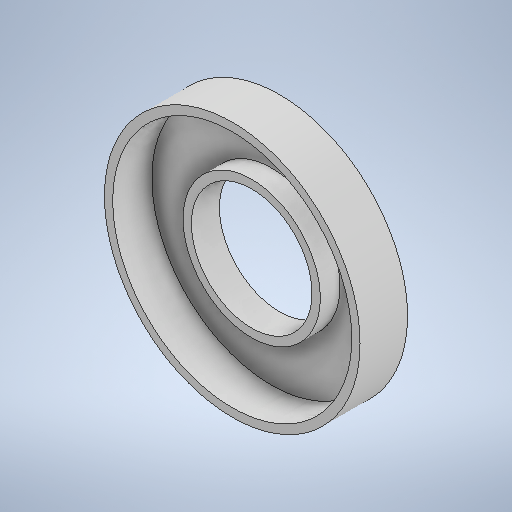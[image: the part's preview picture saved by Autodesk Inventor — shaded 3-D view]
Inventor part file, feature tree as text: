
AUTODESK INVENTOR PART (.ipt)
format: ipt  version: 2025.2 (Build 292293000, 293)  size: 267,776 bytes
history: native  units: in
note: dims shown in document units (in); Inventor stores cm internally (conversion verified against a paired STEP export)
features: extrude x4, sketch x4
ambient origin geometry x8: Origin, YZ Plane, XZ Plane, XY Plane, X Axis, Y Axis, Z Axis, Center Point
bodies: Solid1 (feature_tree)
feature tree (8):
  extrude  "Extrusion1"  Depth=0.1575in TaperAngle=0.0deg
  extrude  "Extrusion2"  Depth=0.7421in
  extrude  "Extrusion3"  Depth=0.1575in
  extrude  "Extrusion4"  Depth=0.374in
  sketch  "Sketch1"  dims[d0=4.8425in d1=0.1575in d2=0.0in]
  sketch  "Sketch2"  dims[d4=0.7421in d5=0.0in d6=2.2835in]
  sketch  "Sketch3"  dims[d7=0.0in d8=0.0in d9=0.1575in]
  sketch  "Sketch4"  dims[d10=0.374in d11=0.0in d12=4.5276in]
